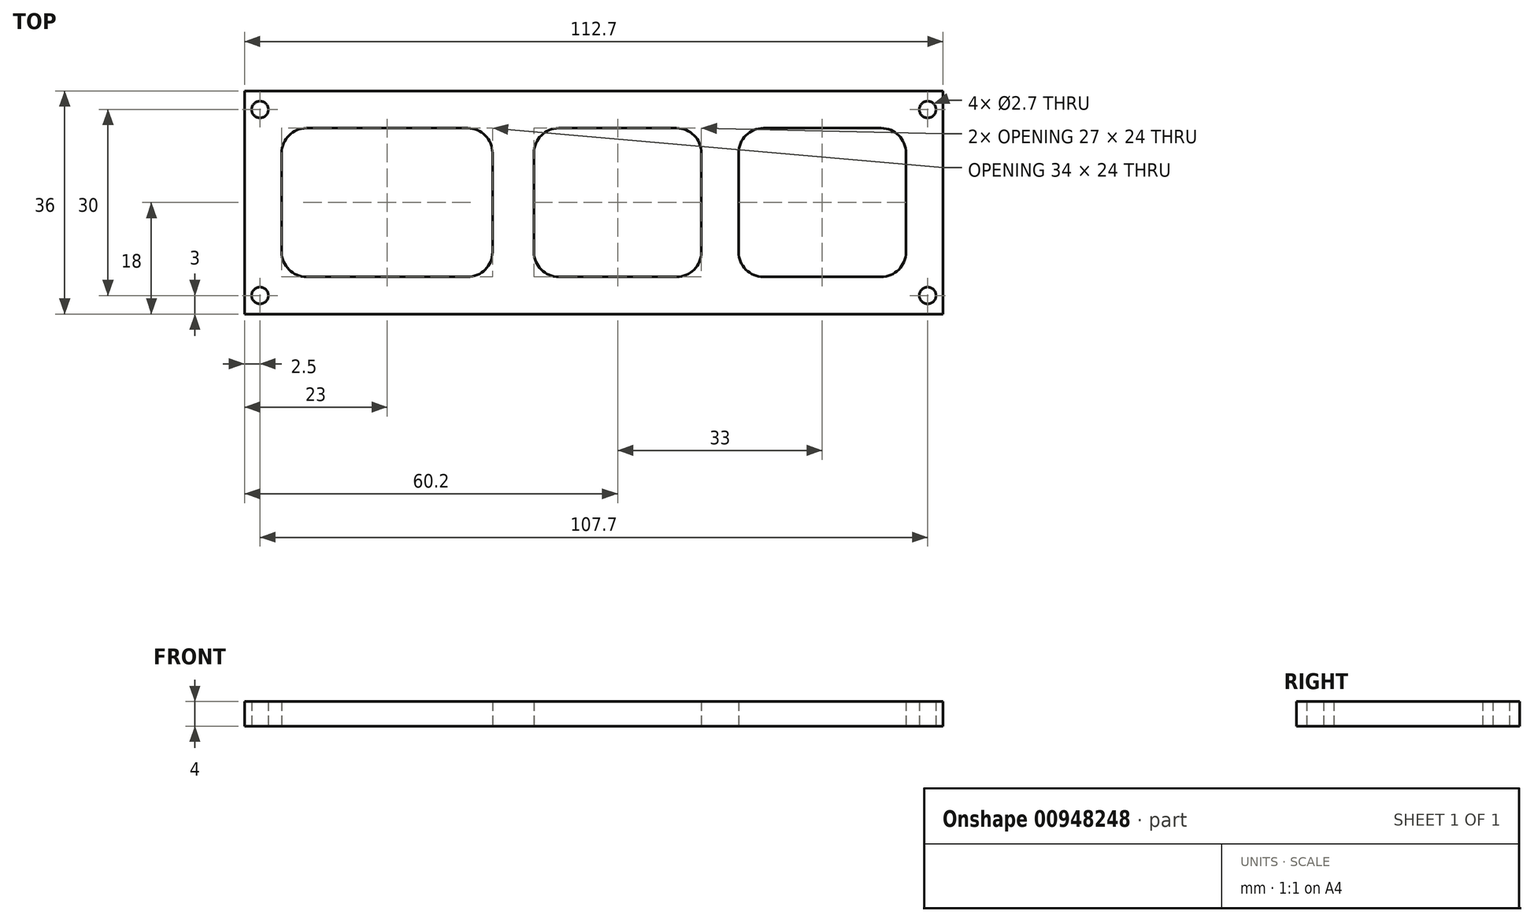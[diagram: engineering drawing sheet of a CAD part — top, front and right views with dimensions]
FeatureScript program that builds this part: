
annotation { "Feature Type Name" : "Feature", "Feature Type Description" : "" }
export const myFeature = defineFeature(function(context is Context, id is Id, definition is map)
    precondition{}
    {
        {
            var Q0;
            Q0=qCreatedBy(makeId("Top.planeOp"),FACE);
            var sketch = newSketch(context, id + "F0", { "sketchPlane" : qUnion([Q0])});
            skLineSegment(sketch, "E0.bottom", {"start": v(56.35, -18) * mm, "end": v(-56.35, -18) * mm});
            skLineSegment(sketch, "E0.top", {"start": v(56.35, 18) * mm, "end": v(-56.35, 18) * mm});
            skLineSegment(sketch, "E0.left", {"start": v(56.35, -18) * mm, "end": v(56.35, 18) * mm});
            skLineSegment(sketch, "E0.right", {"start": v(-56.35, -18) * mm, "end": v(-56.35, 18) * mm});
            skPoint(sketch, "E0.middle", {"position": v(0, 0) * mm});
            skSolve(sketch);
        }
        {
            var Q0;
            Q0=makeQuery(id+"F0.imprint","IMPRINT",FACE,{"disambiguationData":[TD([[makeQuery(id+"F0.imprint","IMPRINT",EDGE,{"derivedFrom":sQuery(id+"F0.wireOp",EDGE,"E0.bottom")}),-1.0]])]});
            extrude(context, id + "F1", {"entities" : qUnion([Q0]), "depth" : 4 * mm, "offsetDistance" : 25 * mm});
        }
        {
            var Q0;
            Q0=makeQuery(id+"F1.opExtrude","CAP_FACE",FACE,{"disambiguationData":[OSD([sQuery(id+"F0.wireOp",EDGE,"E0.bottom"),sQuery(id+"F0.wireOp",EDGE,"E0.top"),sQuery(id+"F0.wireOp",EDGE,"E0.left"),sQuery(id+"F0.wireOp",EDGE,"E0.right")])],"isStart":true});
            var sketch = newSketch(context, id + "F2", { "sketchPlane" : qUnion([Q0])});
            skLineSegment(sketch, "E1", {"start": v(-65.19, 0) * mm, "end": v(58.26, 0) * mm, "construction": true});
            skLineSegment(sketch, "E2", {"start": v(0, 29.35) * mm, "end": v(0, -25.17) * mm, "construction": true});
            skPoint(sketch, "E2.endSnap0", {"position": v(0, -18) * mm});
            skCircle(sketch, "E3", {"center": v(-53.85, 15) * mm, "radius": 1.35 * mm});
            skCircle(sketch, "E4.0.1.0", {"center": v(-53.85, -15) * mm, "radius": 1.35 * mm});
            skCircle(sketch, "E4.1.0.0", {"center": v(53.85, 15) * mm, "radius": 1.35 * mm});
            skCircle(sketch, "E4.1.1.0", {"center": v(53.85, -15) * mm, "radius": 1.35 * mm});
            skLineSegment(sketch, "E4.direction1", {"start": v(-53.85, 15) * mm, "end": v(53.85, 15) * mm, "construction": true});
            skLineSegment(sketch, "E4.direction2", {"start": v(-53.85, 15) * mm, "end": v(-53.85, -15) * mm, "construction": true});
            skSolve(sketch);
        }
        {
            var Q0;
            Q0=makeQuery(id+"F2.imprint","IMPRINT",FACE,{"disambiguationData":[TD([[makeQuery(id+"F2.imprint","IMPRINT",EDGE,{"derivedFrom":sQuery(id+"F2.wireOp",EDGE,"E3")}),1.0]])]});
            var Q1;
            Q1=makeQuery(id+"F2.imprint","IMPRINT",FACE,{"disambiguationData":[TD([[makeQuery(id+"F2.imprint","IMPRINT",EDGE,{"derivedFrom":sQuery(id+"F2.wireOp",EDGE,"E4.0.1.0")}),1.0]])]});
            var Q2;
            Q2=makeQuery(id+"F2.imprint","IMPRINT",FACE,{"disambiguationData":[TD([[makeQuery(id+"F2.imprint","IMPRINT",EDGE,{"derivedFrom":sQuery(id+"F2.wireOp",EDGE,"E4.1.0.0")}),1.0]])]});
            var Q3;
            Q3=makeQuery(id+"F2.imprint","IMPRINT",FACE,{"disambiguationData":[TD([[makeQuery(id+"F2.imprint","IMPRINT",EDGE,{"derivedFrom":sQuery(id+"F2.wireOp",EDGE,"E4.1.1.0")}),1.0]])]});
            extrude(context, id + "F3", {"entities" : qUnion([Q0, Q1, Q2, Q3]), "operationType" : NewBodyOperationType.REMOVE, "endBound" : BoundingType.THROUGH_ALL, "oppositeDirection" : true, "depth" : 5.5 * mm, "offsetDistance" : 25 * mm});
        }
        {
            var Q0;
            Q0=makeQuery(id+"F1.opExtrude","CAP_FACE",FACE,{"disambiguationData":[OSD([sQuery(id+"F0.wireOp",EDGE,"E0.bottom"),sQuery(id+"F0.wireOp",EDGE,"E0.top"),sQuery(id+"F0.wireOp",EDGE,"E0.left"),sQuery(id+"F0.wireOp",EDGE,"E0.right")])],"isStart":true});
            var sketch = newSketch(context, id + "F4", { "sketchPlane" : qUnion([Q0])});
            skLineSegment(sketch, "E5.bottom", {"start": v(-50.35, 12) * mm, "end": v(-16.35, 12) * mm});
            skLineSegment(sketch, "E5.top", {"start": v(-50.35, -12) * mm, "end": v(-16.35, -12) * mm});
            skLineSegment(sketch, "E5.left", {"start": v(-50.35, 12) * mm, "end": v(-50.35, -12) * mm});
            skLineSegment(sketch, "E5.right", {"start": v(-16.35, 12) * mm, "end": v(-16.35, -12) * mm});
            skLineSegment(sketch, "E6.bottom", {"start": v(-9.65, 12) * mm, "end": v(17.35, 12) * mm});
            skLineSegment(sketch, "E6.top", {"start": v(-9.65, -12) * mm, "end": v(17.35, -12) * mm});
            skLineSegment(sketch, "E6.left", {"start": v(-9.65, 12) * mm, "end": v(-9.65, -12) * mm});
            skLineSegment(sketch, "E6.right", {"start": v(17.35, 12) * mm, "end": v(17.35, -12) * mm});
            skLineSegment(sketch, "E7.bottom", {"start": v(23.35, 12) * mm, "end": v(50.35, 12) * mm});
            skLineSegment(sketch, "E7.top", {"start": v(23.35, -12) * mm, "end": v(50.35, -12) * mm});
            skLineSegment(sketch, "E7.left", {"start": v(23.35, 12) * mm, "end": v(23.35, -12) * mm});
            skLineSegment(sketch, "E7.right", {"start": v(50.35, 12) * mm, "end": v(50.35, -12) * mm});
            skSolve(sketch);
        }
        {
            var Q0;
            Q0=qSketchRegion(id+"F4",true);
            extrude(context, id + "F5", {"entities" : qUnion([Q0]), "operationType" : NewBodyOperationType.REMOVE, "endBound" : BoundingType.THROUGH_ALL, "oppositeDirection" : true, "depth" : 25 * mm, "offsetDistance" : 25 * mm});
        }
        {
            var Q0;
            Q0=makeQuery(id+"F5.boolean.opBoolean","COPY",EDGE,{"derivedFrom":makeQuery(id+"F5.opExtrude","SWEPT_EDGE",EDGE,{"disambiguationData":[OSD([sQuery(id+"F4.wireOp",EDGE,"E5.bottom"),sQuery(id+"F4.wireOp",EDGE,"E5.right")])]})});
            var Q1;
            Q1=makeQuery(id+"F5.boolean.opBoolean","COPY",EDGE,{"derivedFrom":makeQuery(id+"F5.opExtrude","SWEPT_EDGE",EDGE,{"disambiguationData":[OSD([sQuery(id+"F4.wireOp",EDGE,"E5.bottom"),sQuery(id+"F4.wireOp",EDGE,"E5.left")])]})});
            var Q2;
            Q2=makeQuery(id+"F5.boolean.opBoolean","COPY",EDGE,{"derivedFrom":makeQuery(id+"F5.opExtrude","SWEPT_EDGE",EDGE,{"disambiguationData":[OSD([sQuery(id+"F4.wireOp",EDGE,"E5.top"),sQuery(id+"F4.wireOp",EDGE,"E5.left")])]})});
            var Q3;
            Q3=makeQuery(id+"F5.boolean.opBoolean","COPY",EDGE,{"derivedFrom":makeQuery(id+"F5.opExtrude","SWEPT_EDGE",EDGE,{"disambiguationData":[OSD([sQuery(id+"F4.wireOp",EDGE,"E5.top"),sQuery(id+"F4.wireOp",EDGE,"E5.right")])]})});
            var Q4;
            Q4=makeQuery(id+"F5.boolean.opBoolean","COPY",EDGE,{"derivedFrom":makeQuery(id+"F5.opExtrude","SWEPT_EDGE",EDGE,{"disambiguationData":[OSD([sQuery(id+"F4.wireOp",EDGE,"ASHmsOBw-3oSF-lJMD-qqwJ-uZuqxBQYEQ6e.bottom"),sQuery(id+"F4.wireOp",EDGE,"ASHmsOBw-3oSF-lJMD-qqwJ-uZuqxBQYEQ6e.left")])]})});
            var Q5;
            Q5=makeQuery(id+"F5.boolean.opBoolean","COPY",EDGE,{"derivedFrom":makeQuery(id+"F5.opExtrude","SWEPT_EDGE",EDGE,{"disambiguationData":[OSD([sQuery(id+"F4.wireOp",EDGE,"E6.bottom"),sQuery(id+"F4.wireOp",EDGE,"E6.left")])]})});
            var Q6;
            Q6=makeQuery(id+"F5.boolean.opBoolean","COPY",EDGE,{"derivedFrom":makeQuery(id+"F5.opExtrude","SWEPT_EDGE",EDGE,{"disambiguationData":[OSD([sQuery(id+"F4.wireOp",EDGE,"E7.bottom"),sQuery(id+"F4.wireOp",EDGE,"E7.left")])]})});
            var Q7;
            Q7=makeQuery(id+"F5.boolean.opBoolean","COPY",EDGE,{"derivedFrom":makeQuery(id+"F5.opExtrude","SWEPT_EDGE",EDGE,{"disambiguationData":[OSD([sQuery(id+"F4.wireOp",EDGE,"E6.top"),sQuery(id+"F4.wireOp",EDGE,"E6.left")])]})});
            var Q8;
            Q8=makeQuery(id+"F5.boolean.opBoolean","COPY",EDGE,{"derivedFrom":makeQuery(id+"F5.opExtrude","SWEPT_EDGE",EDGE,{"disambiguationData":[OSD([sQuery(id+"F4.wireOp",EDGE,"ASHmsOBw-3oSF-lJMD-qqwJ-uZuqxBQYEQ6e.top"),sQuery(id+"F4.wireOp",EDGE,"ASHmsOBw-3oSF-lJMD-qqwJ-uZuqxBQYEQ6e.left")])]})});
            var Q9;
            Q9=makeQuery(id+"F5.boolean.opBoolean","COPY",EDGE,{"derivedFrom":makeQuery(id+"F5.opExtrude","SWEPT_EDGE",EDGE,{"disambiguationData":[OSD([sQuery(id+"F4.wireOp",EDGE,"E6.bottom"),sQuery(id+"F4.wireOp",EDGE,"E6.right")])]})});
            var Q10;
            Q10=makeQuery(id+"F5.boolean.opBoolean","COPY",EDGE,{"derivedFrom":makeQuery(id+"F5.opExtrude","SWEPT_EDGE",EDGE,{"disambiguationData":[OSD([sQuery(id+"F4.wireOp",EDGE,"E7.bottom"),sQuery(id+"F4.wireOp",EDGE,"E7.right")])]})});
            var Q11;
            Q11=makeQuery(id+"F5.boolean.opBoolean","COPY",EDGE,{"derivedFrom":makeQuery(id+"F5.opExtrude","SWEPT_EDGE",EDGE,{"disambiguationData":[OSD([sQuery(id+"F4.wireOp",EDGE,"E7.top"),sQuery(id+"F4.wireOp",EDGE,"E7.right")])]})});
            var Q12;
            Q12=makeQuery(id+"F5.boolean.opBoolean","COPY",EDGE,{"derivedFrom":makeQuery(id+"F5.opExtrude","SWEPT_EDGE",EDGE,{"disambiguationData":[OSD([sQuery(id+"F4.wireOp",EDGE,"E7.top"),sQuery(id+"F4.wireOp",EDGE,"E7.left")])]})});
            var Q13;
            Q13=makeQuery(id+"F5.boolean.opBoolean","COPY",EDGE,{"derivedFrom":makeQuery(id+"F5.opExtrude","SWEPT_EDGE",EDGE,{"disambiguationData":[OSD([sQuery(id+"F4.wireOp",EDGE,"ASHmsOBw-3oSF-lJMD-qqwJ-uZuqxBQYEQ6e.bottom"),sQuery(id+"F4.wireOp",EDGE,"ASHmsOBw-3oSF-lJMD-qqwJ-uZuqxBQYEQ6e.right")])]})});
            var Q14;
            Q14=makeQuery(id+"F5.boolean.opBoolean","COPY",EDGE,{"derivedFrom":makeQuery(id+"F5.opExtrude","SWEPT_EDGE",EDGE,{"disambiguationData":[OSD([sQuery(id+"F4.wireOp",EDGE,"ASHmsOBw-3oSF-lJMD-qqwJ-uZuqxBQYEQ6e.top"),sQuery(id+"F4.wireOp",EDGE,"ASHmsOBw-3oSF-lJMD-qqwJ-uZuqxBQYEQ6e.right")])]})});
            var Q15;
            Q15=makeQuery(id+"F5.boolean.opBoolean","COPY",EDGE,{"derivedFrom":makeQuery(id+"F5.opExtrude","SWEPT_EDGE",EDGE,{"disambiguationData":[OSD([sQuery(id+"F4.wireOp",EDGE,"E6.top"),sQuery(id+"F4.wireOp",EDGE,"E6.right")])]})});
            fillet(context, id + "F6", {"entities" : qUnion([Q0, Q1, Q2, Q3, Q4, Q5, Q6, Q7, Q8, Q9, Q10, Q11, Q12, Q13, Q14, Q15]), "radius" : 4 * mm, "tangentPropagation" : true, "allowEdgeOverflow" : false});
        }
    });
